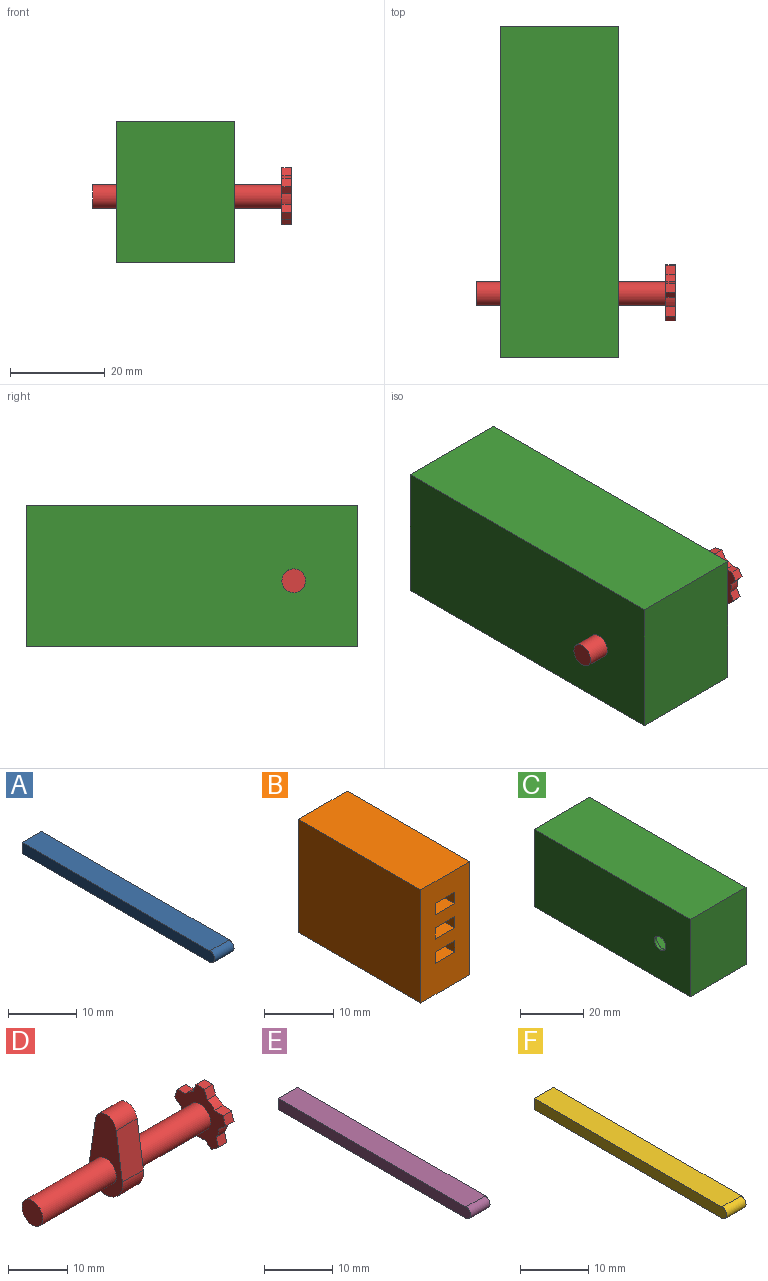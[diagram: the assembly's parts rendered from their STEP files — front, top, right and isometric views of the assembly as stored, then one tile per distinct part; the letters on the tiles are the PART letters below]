
ASSEMBLY  parts=6 mates=4
PART A: 6 faces, bbox 4x40x2 mm
  f0: plane 39x4mm, normal (0,0,1), area 156mm2, adj f2,f3,f4,f5
  f1: plane 39x4mm, normal (0,0,-1), area 156mm2, adj f2,f3,f4,f5
  f2: plane 40x2mm, normal (1,0,0), area 79.6mm2, adj f0,f1,f3,f5
  f3: plane 4x2mm, normal (0,1,0), area 8mm2, adj f0,f1,f2,f4
  f4: plane 40x2mm, normal (-1,0,0), area 79.6mm2, adj f0,f1,f3,f5
  f5: cylinder r=1mm len=4mm, axis (1,0,0), area 12.6mm2, adj f0,f1,f2,f4
PART B: 18 faces, bbox 10x25x20 mm
  f0: plane 25x20mm, normal (1,0,0), area 500mm2, adj f1,f3,f4,f5
  f1: plane 25x10mm, normal (0,0,1), area 250mm2, adj f0,f2,f4,f5
  f2: plane 25x20mm, normal (-1,0,0), area 500mm2, adj f1,f3,f4,f5
  f3: plane 25x10mm, normal (0,0,-1), area 250mm2, adj f0,f2,f4,f5
  f4: plane 20x10mm, normal (0,-1,0), area 176mm2, adj f0,f1,f2,f3,f6,f7,f8,f9
  f5: plane 20x10mm, normal (0,1,0), area 176mm2, adj f0,f1,f2,f3,f6,f7,f8,f9
  f6: plane 25x4mm, normal (0,0,-1), area 100mm2, adj f4,f5,f8,f9
  f7: plane 25x4mm, normal (0,0,1), area 100mm2, adj f4,f5,f8,f9
  f8: plane 25x2mm, normal (-1,0,0), area 50mm2, adj f4,f5,f6,f7
  f9: plane 25x2mm, normal (1,0,0), area 50mm2, adj f4,f5,f6,f7
  f10: plane 25x4mm, normal (0,0,-1), area 100mm2, adj f4,f5,f12,f13
  f11: plane 25x4mm, normal (0,0,1), area 100mm2, adj f4,f5,f12,f13
  f12: plane 25x2mm, normal (-1,0,0), area 50mm2, adj f4,f5,f10,f11
  f13: plane 25x2mm, normal (1,0,0), area 50mm2, adj f4,f5,f10,f11
  f14: plane 25x4mm, normal (0,0,-1), area 100mm2, adj f4,f5,f16,f17
  f15: plane 25x4mm, normal (0,0,1), area 100mm2, adj f4,f5,f16,f17
  f16: plane 25x2mm, normal (-1,0,0), area 50mm2, adj f4,f5,f14,f15
  f17: plane 25x2mm, normal (1,0,0), area 50mm2, adj f4,f5,f14,f15
PART C: 14 faces, bbox 25x70x30 mm
  f0: plane 26x23mm, normal (0,-1,0), area 598mm2, adj f1,f3,f4,f5
  f1: plane 66x23mm, normal (0,0,-1), area 1518mm2, adj f0,f2,f4,f5
  f2: plane 26x23mm, normal (0,1,0), area 598mm2, adj f1,f3,f4,f5
  f3: plane 66x23mm, normal (0,0,1), area 1518mm2, adj f0,f2,f4,f5
  f4: plane 66x26mm, normal (-1,0,0), area 1696.4mm2, adj f0,f1,f2,f3,f7
  f5: plane 66x26mm, normal (1,0,0), area 1696.4mm2, adj f0,f1,f2,f3,f6
  f6: cylinder r=2.5mm len=5mm, axis (-1,0,0), area 15.7mm2, adj f5,f13
  f7: cylinder r=2.5mm len=5mm, axis (-1,0,0), area 15.7mm2, adj f4,f12
  f8: plane 70x25mm, normal (0,0,-1), area 1750mm2, adj f9,f11,f12,f13
  f9: plane 30x25mm, normal (0,1,0), area 750mm2, adj f8,f10,f12,f13
  f10: plane 70x25mm, normal (0,0,1), area 1750mm2, adj f9,f11,f12,f13
  f11: plane 30x25mm, normal (0,-1,0), area 750mm2, adj f8,f10,f12,f13
  f12: plane 70x30mm, normal (1,0,0), area 2080.4mm2, adj f7,f8,f9,f10,f11
  f13: plane 70x30mm, normal (-1,0,0), area 2080.4mm2, adj f6,f8,f9,f10,f11
PART D: 31 faces, bbox 42x12.1x17.1 mm
  f0: cylinder r=2.5mm len=17.5mm, axis (-1,0,0), area 274.9mm2, adj f7,f27
  f1: cylinder r=4.5mm len=2.07mm, axis (1,0,0), area 4.4mm2, adj f5,f7,f10,f13
  f2: cylinder r=4.5mm len=2mm, axis (1,0,0), area 4.4mm2, adj f5,f7,f12,f16
  f3: cylinder r=4.5mm len=2mm, axis (1,0,0), area 4.4mm2, adj f5,f7,f15,f19
  f4: cylinder r=4.5mm len=2.07mm, axis (1,0,0), area 4.4mm2, adj f5,f7,f18,f20
  f5: plane 12.13x11.54mm, normal (1,0,0), area 85.1mm2, adj f1,f2,f3,f4,f6,f8,f9,f10
  f6: cylinder r=4.5mm len=2.18mm, axis (1,0,0), area 4.4mm2, adj f5,f7,f9,f22
  f7: plane 12.13x11.54mm, normal (-1,0,0), area 65.5mm2, adj f0,f1,f2,f3,f4,f6,f8,f9
  f8: plane 2x1.62mm, normal (0,0.59,-0.81), area 4mm2, adj f5,f7,f9,f10
  f9: plane 2x1.66mm, normal (0,-0.56,-0.83), area 4mm2, adj f5,f6,f7,f8
  f10: plane 2x1.92mm, normal (0,0.96,0.28), area 4mm2, adj f1,f5,f7,f8
  f11: plane 2x1.9mm, normal (0,0.95,0.31), area 4mm2, adj f5,f7,f12,f13
  f12: plane 2x2mm, normal (0,0.03,1), area 4mm2, adj f2,f5,f7,f11
  f13: plane 2x1.58mm, normal (0,0.62,-0.79), area 4mm2, adj f1,f5,f7,f11
  f14: plane 2x2mm, normal (0,0,1), area 4mm2, adj f5,f7,f15,f16
  f15: plane 2x1.88mm, normal (0,-0.94,0.34), area 4mm2, adj f3,f5,f7,f14
  f16: plane 2x1.88mm, normal (0,0.94,0.34), area 4mm2, adj f2,f5,f7,f14
  f17: plane 2x1.9mm, normal (0,-0.95,0.31), area 4mm2, adj f5,f7,f18,f19
  f18: plane 2x1.58mm, normal (0,-0.62,-0.79), area 4mm2, adj f4,f5,f7,f17
  f19: plane 2x2mm, normal (0,-0.03,1), area 4mm2, adj f3,f5,f7,f17
  f20: plane 2x1.92mm, normal (0,-0.96,0.28), area 4mm2, adj f4,f5,f7,f21
  f21: plane 2x1.62mm, normal (0,-0.59,-0.81), area 4mm2, adj f5,f7,f20,f22
  f22: plane 2x1.66mm, normal (0,0.56,-0.83), area 4mm2, adj f5,f6,f7,f21
  f23: cylinder r=2.5mm len=5mm, axis (-1,0,0), area 35.5mm2, adj f24,f26,f27,f28
  f24: plane 9.89x5mm, normal (0,-0.99,0.15), area 50mm2, adj f23,f25,f27,f28
  f25: cylinder r=4mm len=8mm, axis (-1,0,0), area 68.8mm2, adj f24,f26,f27,f28
  f26: plane 9.89x5mm, normal (0,0.99,0.15), area 50mm2, adj f23,f25,f27,f28
  f27: plane 16.61x8mm, normal (1,0,0), area 81.8mm2, adj f0,f23,f24,f25,f26
  f28: plane 16.61x8mm, normal (-1,0,0), area 81.8mm2, adj f23,f24,f25,f26,f30
  f29: plane 5x5mm, normal (-1,0,0), area 19.6mm2, adj f30
  f30: cylinder r=2.5mm len=17.5mm, axis (-1,0,0), area 274.9mm2, adj f28,f29
PART E: 6 faces, bbox 4x40x2 mm
  f0: plane 39x4mm, normal (0,0,1), area 156mm2, adj f2,f3,f4,f5
  f1: plane 39x4mm, normal (0,0,-1), area 156mm2, adj f2,f3,f4,f5
  f2: plane 40x2mm, normal (1,0,0), area 79.6mm2, adj f0,f1,f3,f5
  f3: plane 4x2mm, normal (0,1,0), area 8mm2, adj f0,f1,f2,f4
  f4: plane 40x2mm, normal (-1,0,0), area 79.6mm2, adj f0,f1,f3,f5
  f5: cylinder r=1mm len=4mm, axis (1,0,0), area 12.6mm2, adj f0,f1,f2,f4
PART F: 6 faces, bbox 4x40x2 mm
  f0: plane 39x4mm, normal (0,0,1), area 156mm2, adj f2,f3,f4,f5
  f1: plane 39x4mm, normal (0,0,-1), area 156mm2, adj f2,f3,f4,f5
  f2: plane 40x2mm, normal (1,0,0), area 79.6mm2, adj f0,f1,f3,f5
  f3: plane 4x2mm, normal (0,1,0), area 8mm2, adj f0,f1,f2,f4
  f4: plane 40x2mm, normal (-1,0,0), area 79.6mm2, adj f0,f1,f3,f5
  f5: cylinder r=1mm len=4mm, axis (1,0,0), area 12.6mm2, adj f0,f1,f2,f4
PLACE A rot(axis=(0,1,0.07),0deg) t=(0,3.46,0)mm
PLACE B at identity fixed
PLACE C at identity fixed
PLACE D rot(axis=(-1,0,0),155.9deg) t=(2.5,-53.96,-9.54)mm
PLACE E t=(0,-3.96,0)mm
PLACE F t=(0,3.65,0)mm
MATE slider E.f3 <-> B.f5  axis (0,1,0) through (2,16.04,1)mm
MATE slider F.f3 <-> B.f5  axis (0,1,0) through (2,23.65,4.3)mm
MATE revolute D.f0 <-> C.f6  axis (-1,0,0) through (-17.5,-28,1)mm
MATE slider A.f3 <-> B.f5  axis (0,1,0) through (2,23.46,8.6)mm
